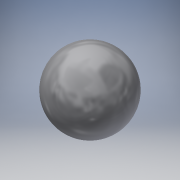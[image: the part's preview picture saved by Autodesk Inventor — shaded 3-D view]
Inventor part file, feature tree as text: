
AUTODESK INVENTOR PART (.ipt)
format: ipt  version: 2019 (Build 230136000, 136)  size: 140,800 bytes
history: mixed  units: mm
features: revolve x1, imported_body x1
ambient origin geometry x8: Origin, YZ Plane, XZ Plane, XY Plane, X Axis, Y Axis, Z Axis, Center Point
bodies: Solid1 (imported_parasolid)
feature tree (2):
  revolve  "Revolve1"  [1 undecoded]
  imported_body  NMx_Import_Brep_tag  [imported B-rep: ~1 faces, bbox_mm=None]
note: 1 required parameter value undecoded (feature->parameter linkage not recoverable at this tier; creation-order binding heuristic only, values carry confidence <= 0.55)
